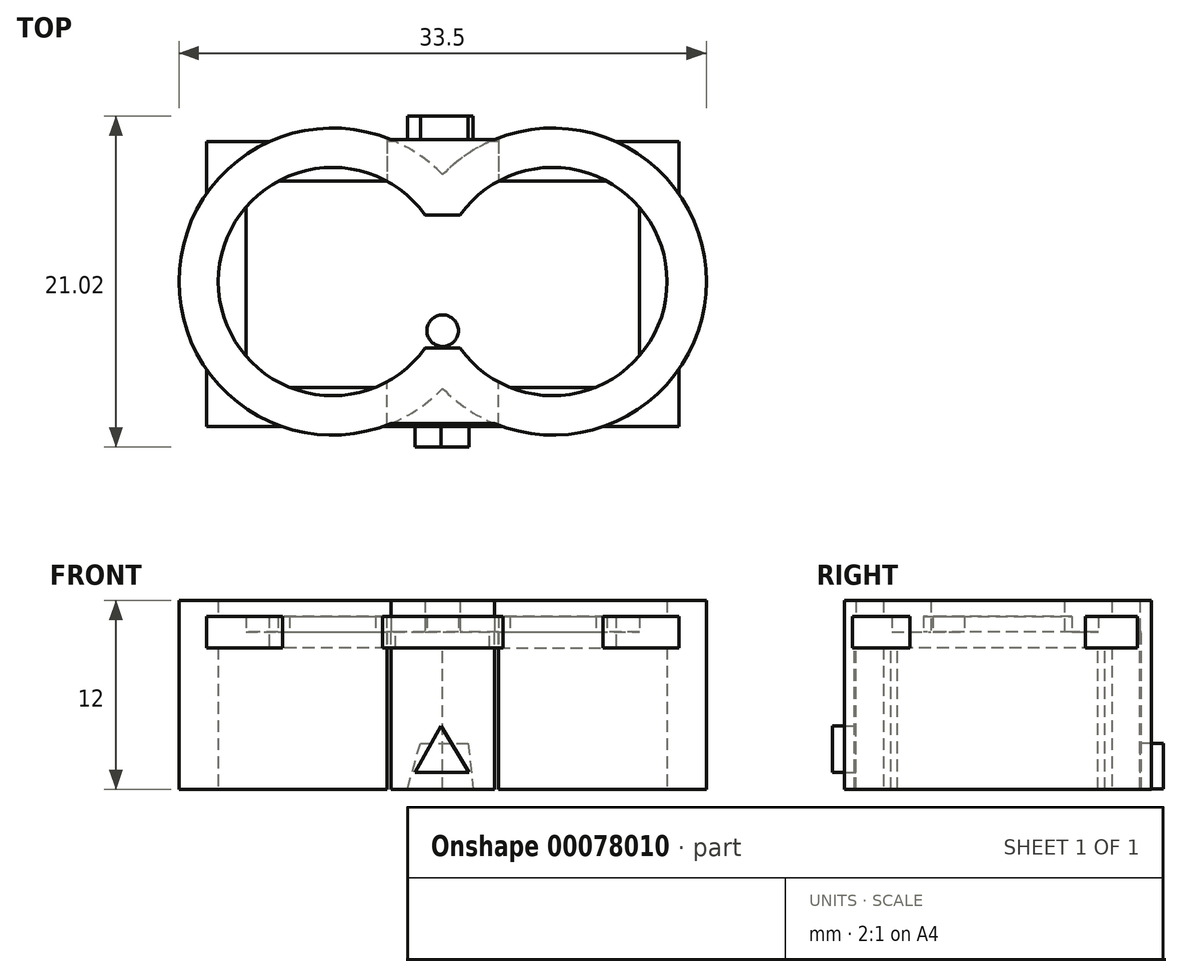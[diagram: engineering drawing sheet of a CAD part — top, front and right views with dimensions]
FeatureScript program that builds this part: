
annotation { "Feature Type Name" : "Feature", "Feature Type Description" : "" }
export const myFeature = defineFeature(function(context is Context, id is Id, definition is map)
    precondition{}
    {
        {
            var Q0;
            Q0=qCreatedBy(makeId("Top.planeOp"),FACE);
            var sketch = newSketch(context, id + "F0", { "sketchPlane" : qUnion([Q0])});
            skLineSegment(sketch, "E0.bottom", {"start": v(0, 13.1) * mm, "end": v(25, 13.1) * mm});
            skLineSegment(sketch, "E0.top", {"start": v(0, 0) * mm, "end": v(25, 0) * mm});
            skLineSegment(sketch, "E0.left", {"start": v(0, 13.1) * mm, "end": v(0, 0) * mm});
            skLineSegment(sketch, "E0.right", {"start": v(25, 13.1) * mm, "end": v(25, 0) * mm});
            skLineSegment(sketch, "E1", {"start": v(12.5, 13.1) * mm, "end": v(12.5, 0) * mm, "construction": true});
            skCircle(sketch, "E2", {"center": v(12.5, 3.6) * mm, "radius": 1 * mm});
            skLineSegment(sketch, "E3.0", {"start": v(-2.5, 15.6) * mm, "end": v(27.5, 15.6) * mm});
            skLineSegment(sketch, "E3.1", {"start": v(-2.5, 15.6) * mm, "end": v(-2.5, -2.5) * mm});
            skLineSegment(sketch, "E3.2", {"start": v(-2.5, -2.5) * mm, "end": v(27.5, -2.5) * mm});
            skLineSegment(sketch, "E3.3", {"start": v(27.5, 15.6) * mm, "end": v(27.5, -2.5) * mm});
            skLineSegment(sketch, "E4", {"start": v(5.5, 6.72) * mm, "end": v(12.5, 6.72) * mm, "construction": true});
            skLineSegment(sketch, "E5", {"start": v(12.5, 6.72) * mm, "end": v(19.5, 6.72) * mm, "construction": true});
            skArc(sketch, "E6", {"start": v(12.5, 8.6) * mm, "mid": v(-1.75, 6.72) * mm, "end": v(12.5, 4.83) * mm});
            skArc(sketch, "E7", {"start": v(12.5, 4.83) * mm, "mid": v(12.75, 6.72) * mm, "end": v(12.5, 8.6) * mm});
            skArc(sketch, "E8", {"start": v(12.5, 4.83) * mm, "mid": v(26.75, 6.72) * mm, "end": v(12.5, 8.6) * mm});
            skArc(sketch, "E9", {"start": v(12.5, 8.6) * mm, "mid": v(12.25, 6.72) * mm, "end": v(12.5, 4.83) * mm});
            skArc(sketch, "E10.0", {"start": v(12.5, 13.5) * mm, "mid": v(-4.25, 6.72) * mm, "end": v(12.5, -0.07) * mm});
            skArc(sketch, "E10.1", {"start": v(12.5, -0.07) * mm, "mid": v(29.25, 6.72) * mm, "end": v(12.5, 13.5) * mm});
            skLineSegment(sketch, "E11", {"start": v(8.97, 15.83) * mm, "end": v(8.97, 13.09) * mm});
            skLineSegment(sketch, "E12.MirrorCS", {"start": v(8.97, -2.4) * mm, "end": v(8.97, 0.35) * mm});
            skLineSegment(sketch, "E13.MirrorCS", {"start": v(16.03, 15.83) * mm, "end": v(16.03, 13.09) * mm});
            skLineSegment(sketch, "E14.MirrorCS", {"start": v(16.03, -2.4) * mm, "end": v(16.03, 0.35) * mm});
            skSolve(sketch);
        }
        {
            var Q0;
            Q0=qCreatedBy(makeId("Top.planeOp"),FACE);
            var sketch = newSketch(context, id + "F1", { "sketchPlane" : qUnion([Q0])});
            skLineSegment(sketch, "E15.0", {"start": v(0, 13.1) * mm, "end": v(25, 13.1) * mm});
            skLineSegment(sketch, "E16.0", {"start": v(0, 13.1) * mm, "end": v(0, 0) * mm});
            skLineSegment(sketch, "E17.0", {"start": v(0, 0) * mm, "end": v(25, 0) * mm});
            skLineSegment(sketch, "E18.0", {"start": v(25, 13.1) * mm, "end": v(25, 0) * mm});
            skLineSegment(sketch, "E19.0", {"start": v(27.5, 15.6) * mm, "end": v(27.5, -2.5) * mm});
            skLineSegment(sketch, "E20.0", {"start": v(-2.5, 15.6) * mm, "end": v(27.5, 15.6) * mm});
            skLineSegment(sketch, "E21.0", {"start": v(-2.5, -2.5) * mm, "end": v(27.5, -2.5) * mm});
            skLineSegment(sketch, "E22.0", {"start": v(-2.5, 15.6) * mm, "end": v(-2.5, -2.5) * mm});
            skCircle(sketch, "E23.0", {"center": v(12.5, 3.6) * mm, "radius": 1 * mm});
            skSolve(sketch);
        }
        {
            var Q0;
            Q0=makeQuery(id+"F1.imprint","IMPRINT",FACE,{"disambiguationData":[TD([[makeQuery(id+"F1.imprint","IMPRINT",EDGE,{"derivedFrom":sQuery(id+"F1.wireOp",EDGE,"E15.0")}),-1.0]])]});
            var Q1;
            Q1=makeQuery(id+"F1.imprint","IMPRINT",FACE,{"disambiguationData":[TD([[makeQuery(id+"F1.imprint","IMPRINT",EDGE,{"derivedFrom":sQuery(id+"F1.wireOp",EDGE,"E23.0")}),1.0]])]});
            var Q2;
            Q2=makeQuery(id+"F1.imprint","IMPRINT",FACE,{"disambiguationData":[TD([[makeQuery(id+"F1.imprint","IMPRINT",EDGE,{"derivedFrom":sQuery(id+"F1.wireOp",EDGE,"E15.0")}),1.0]])]});
            extrude(context, id + "F2", {"entities" : qUnion([Q0, Q1, Q2]), "oppositeDirection" : true, "depth" : 1 * mm});
        }
        {
            var Q0;
            Q0=makeQuery(id+"F1.imprint","IMPRINT",FACE,{"disambiguationData":[TD([[makeQuery(id+"F1.imprint","IMPRINT",EDGE,{"derivedFrom":sQuery(id+"F1.wireOp",EDGE,"E15.0")}),1.0]])]});
            var Q1;
            Q1=makeQuery(id+"F1.imprint","IMPRINT",FACE,{"disambiguationData":[TD([[makeQuery(id+"F1.imprint","IMPRINT",EDGE,{"derivedFrom":sQuery(id+"F1.wireOp",EDGE,"E23.0")}),1.0]])]});
            extrude(context, id + "F3", {"entities" : qUnion([Q0, Q1]), "operationType" : NewBodyOperationType.ADD, "depth" : 1 * mm});
        }
        {
            var Q0;
            Q0=qCreatedBy(makeId("Top.planeOp"),FACE);
            var sketch = newSketch(context, id + "F4", { "sketchPlane" : qUnion([Q0])});
            skArc(sketch, "E24.0", {"start": v(12.5, 13.5) * mm, "mid": v(-4.25, 6.72) * mm, "end": v(12.5, -0.07) * mm});
            skLineSegment(sketch, "E25.0", {"start": v(8.97, 15.83) * mm, "end": v(8.97, 13.09) * mm});
            skArc(sketch, "E26.0", {"start": v(12.5, 8.6) * mm, "mid": v(-1.75, 6.72) * mm, "end": v(12.5, 4.83) * mm});
            skLineSegment(sketch, "E27.0", {"start": v(16.03, 15.83) * mm, "end": v(16.03, 13.09) * mm});
            skArc(sketch, "E28.0", {"start": v(12.5, -0.07) * mm, "mid": v(29.25, 6.72) * mm, "end": v(12.5, 13.5) * mm});
            skArc(sketch, "E29.0", {"start": v(12.5, 4.83) * mm, "mid": v(26.75, 6.72) * mm, "end": v(12.5, 8.6) * mm});
            skLineSegment(sketch, "E30.0", {"start": v(16.03, -2.4) * mm, "end": v(16.03, 0.35) * mm});
            skLineSegment(sketch, "E31.0", {"start": v(8.97, -2.4) * mm, "end": v(8.97, 0.35) * mm});
            skLineSegment(sketch, "E32", {"start": v(5.5, 6.72) * mm, "end": v(19.5, 6.72) * mm});
            skLineSegment(sketch, "E33", {"start": v(11.38, 10.95) * mm, "end": v(13.62, 10.95) * mm});
            skLineSegment(sketch, "E34.MirrorCS", {"start": v(11.38, 2.48) * mm, "end": v(13.62, 2.48) * mm});
            skLineSegment(sketch, "E35", {"start": v(9.22, 15.73) * mm, "end": v(15.78, 15.73) * mm});
            skLineSegment(sketch, "E36.MirrorCS", {"start": v(9.22, -2.3) * mm, "end": v(15.78, -2.3) * mm});
            skSolve(sketch);
        }
        {
            var Q0;
            {var subQ1=sQuery(id+"F4.wireOp",EDGE,"E25.0");Q0=makeQuery(id+"F4.imprint","IMPRINT",FACE,{"disambiguationData":[TD([[makeQuery(id+"F4.imprint","IMPRINT",EDGE,{"derivedFrom":subQ1}),1.0]])]});}
            var Q1;
            {var subQ3=sQuery(id+"F4.wireOp",EDGE,"E35");Q1=makeQuery(id+"F4.imprint","IMPRINT",FACE,{"disambiguationData":[TD([[makeQuery(id+"F4.imprint","IMPRINT",EDGE,{"derivedFrom":subQ3}),-1.0]])]});}
            var Q2;
            {var subQ0=sQuery(id+"F4.wireOp",EDGE,"E25.0");Q2=makeQuery(id+"F4.imprint","IMPRINT",FACE,{"disambiguationData":[TD([[makeQuery(id+"F4.imprint","IMPRINT",EDGE,{"derivedFrom":subQ0}),-1.0]])]});}
            var Q3;
            {var subQ0=sQuery(id+"F4.wireOp",EDGE,"E27.0");Q3=makeQuery(id+"F4.imprint","IMPRINT",FACE,{"disambiguationData":[TD([[makeQuery(id+"F4.imprint","IMPRINT",EDGE,{"derivedFrom":subQ0}),1.0]])]});}
            var Q4;
            {var subQ9=sQuery(id+"F4.wireOp",EDGE,"E30.0");Q4=makeQuery(id+"F4.imprint","IMPRINT",FACE,{"disambiguationData":[TD([[makeQuery(id+"F4.imprint","IMPRINT",EDGE,{"derivedFrom":subQ9}),1.0]])]});}
            var Q5;
            {var subQ3=sQuery(id+"F4.wireOp",EDGE,"E36.MirrorCS");Q5=makeQuery(id+"F4.imprint","IMPRINT",FACE,{"disambiguationData":[TD([[makeQuery(id+"F4.imprint","IMPRINT",EDGE,{"derivedFrom":subQ3}),1.0]])]});}
            extrude(context, id + "F5", {"entities" : qUnion([Q0, Q1, Q2, Q3, Q4, Q5]), "depth" : 2 * mm});
        }
        {
            var Q0;
            {var subQ3=sQuery(id+"F4.wireOp",EDGE,"E36.MirrorCS");Q0=makeQuery(id+"F4.imprint","IMPRINT",FACE,{"disambiguationData":[TD([[makeQuery(id+"F4.imprint","IMPRINT",EDGE,{"derivedFrom":subQ3}),1.0]])]});}
            var Q1;
            {var subQ0=sQuery(id+"F4.wireOp",EDGE,"E25.0");Q1=makeQuery(id+"F4.imprint","IMPRINT",FACE,{"disambiguationData":[TD([[makeQuery(id+"F4.imprint","IMPRINT",EDGE,{"derivedFrom":subQ0}),-1.0]])]});}
            var Q2;
            {var subQ0=sQuery(id+"F4.wireOp",EDGE,"E27.0");Q2=makeQuery(id+"F4.imprint","IMPRINT",FACE,{"disambiguationData":[TD([[makeQuery(id+"F4.imprint","IMPRINT",EDGE,{"derivedFrom":subQ0}),1.0]])]});}
            var Q3;
            {var subQ3=sQuery(id+"F4.wireOp",EDGE,"E35");Q3=makeQuery(id+"F4.imprint","IMPRINT",FACE,{"disambiguationData":[TD([[makeQuery(id+"F4.imprint","IMPRINT",EDGE,{"derivedFrom":subQ3}),-1.0]])]});}
            extrude(context, id + "F6", {"entities" : qUnion([Q0, Q1, Q2, Q3]), "operationType" : NewBodyOperationType.ADD, "oppositeDirection" : true, "depth" : 10 * mm});
        }
        {
            var Q0;
            {var subQ0=sQuery(id+"F4.wireOp",EDGE,"E36.MirrorCS");Q0=makeQuery(id+"F6.boolean.opBoolean","MERGE",FACE,{"derivedFrom":[makeQuery(id+"F5.opExtrude","SWEPT_FACE",FACE,{"disambiguationData":[OSD([subQ0])]}),makeQuery(id+"F6.opExtrude","SWEPT_FACE",FACE,{"disambiguationData":[OSD([subQ0])]})]});}
            var sketch = newSketch(context, id + "F7", { "sketchPlane" : qUnion([Q0])});
            skLineSegment(sketch, "E37", {"start": v(12.4, -5.98) * mm, "end": v(10.76, -8.92) * mm});
            skLineSegment(sketch, "E38", {"start": v(10.76, -8.92) * mm, "end": v(14.18, -8.92) * mm});
            skLineSegment(sketch, "E39", {"start": v(14.18, -8.92) * mm, "end": v(12.4, -5.98) * mm});
            skSolve(sketch);
        }
        {
            var Q0;
            Q0 = qSketchRegion(id + "F7", true);
            extrude(context, id + "F8", {"entities" : qUnion([Q0]), "operationType" : NewBodyOperationType.ADD, "depth" : 1.5 * mm});
        }
        {
            var Q0;
            {var subQ0=sQuery(id+"F4.wireOp",EDGE,"E35");Q0=makeQuery(id+"F6.boolean.opBoolean","MERGE",FACE,{"derivedFrom":[makeQuery(id+"F5.opExtrude","SWEPT_FACE",FACE,{"disambiguationData":[OSD([subQ0])]}),makeQuery(id+"F6.opExtrude","SWEPT_FACE",FACE,{"disambiguationData":[OSD([subQ0])]})]});}
            var sketch = newSketch(context, id + "F9", { "sketchPlane" : qUnion([Q0])});
            skLineSegment(sketch, "E40", {"start": v(-14.44, -9.97) * mm, "end": v(-10.26, -9.97) * mm});
            skLineSegment(sketch, "E41", {"start": v(-10.26, -9.97) * mm, "end": v(-11.08, -7.06) * mm});
            skLineSegment(sketch, "E42", {"start": v(-11.08, -7.06) * mm, "end": v(-14.11, -7.06) * mm});
            skLineSegment(sketch, "E43", {"start": v(-14.11, -7.06) * mm, "end": v(-14.44, -9.97) * mm});
            skLineSegment(sketch, "E44.0", {"start": v(-9.22, -10) * mm, "end": v(-15.78, -10) * mm});
            skSolve(sketch);
        }
        {
            var Q0;
            Q0 = qSketchRegion(id + "F9", true);
            extrude(context, id + "F10", {"entities" : qUnion([Q0]), "operationType" : NewBodyOperationType.ADD, "depth" : 1.5 * mm});
        }
    });
